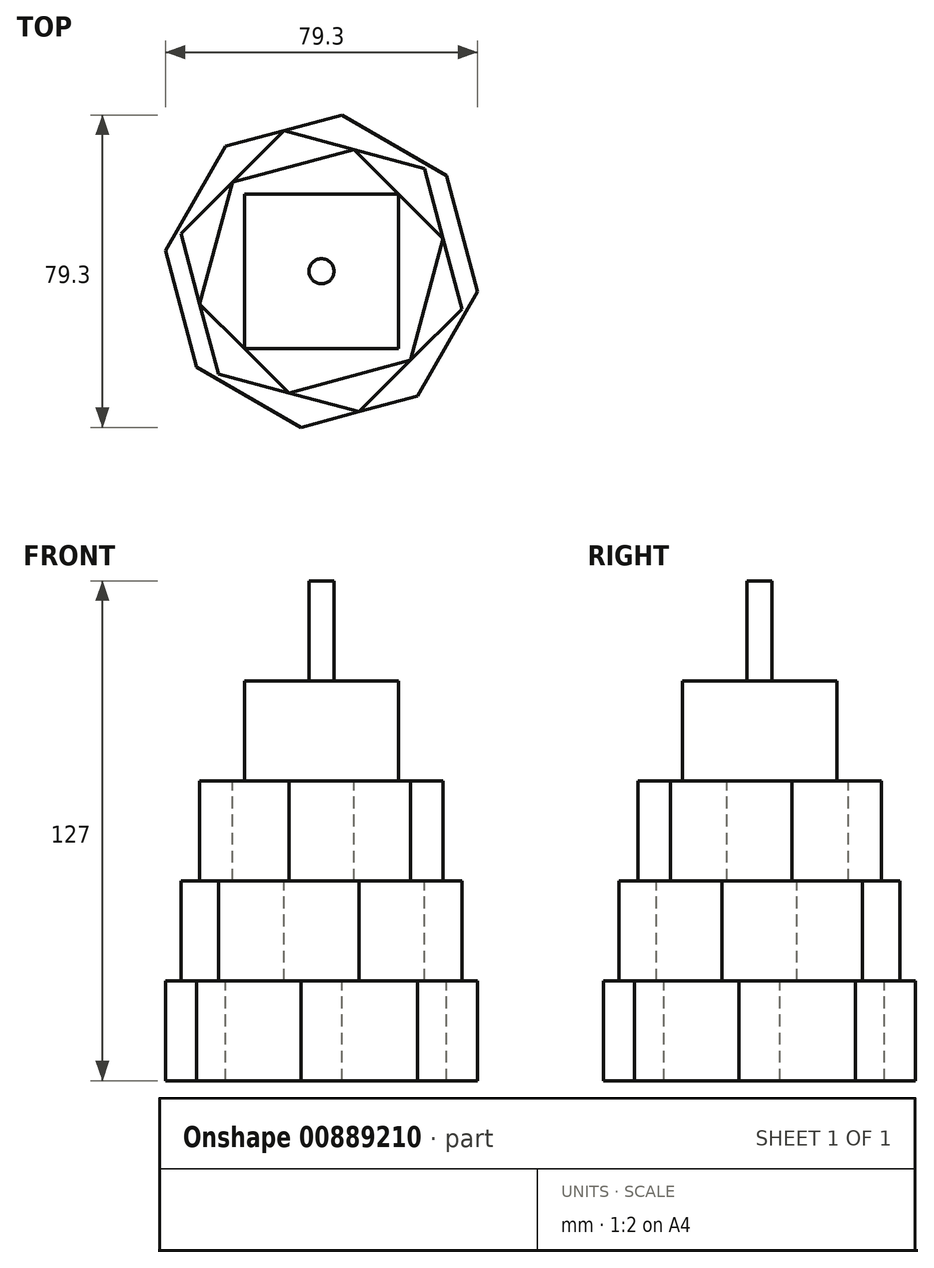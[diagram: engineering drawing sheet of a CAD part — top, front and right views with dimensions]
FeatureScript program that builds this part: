
annotation { "Feature Type Name" : "Feature", "Feature Type Description" : "" }
export const myFeature = defineFeature(function(context is Context, id is Id, definition is map)
    precondition{}
    {
        {
            var Q0;
            Q0=qCreatedBy(makeId("Top.planeOp"),FACE);
            var sketch = newSketch(context, id + "F0", { "sketchPlane" : qUnion([Q0])});
            skLineSegment(sketch, "E0.bottom", {"start": v(19.6, 19.6) * mm, "end": v(-19.6, 19.6) * mm});
            skLineSegment(sketch, "E0.top", {"start": v(19.6, -19.6) * mm, "end": v(-19.6, -19.6) * mm});
            skLineSegment(sketch, "E0.left", {"start": v(19.6, 19.6) * mm, "end": v(19.6, -19.6) * mm});
            skLineSegment(sketch, "E0.right", {"start": v(-19.6, 19.6) * mm, "end": v(-19.6, -19.6) * mm});
            skLineSegment(sketch, "E1.0", {"start": v(8.28, 30.9) * mm, "end": v(30.9, 8.28) * mm});
            skLineSegment(sketch, "E1.1", {"start": v(30.9, 8.28) * mm, "end": v(22.63, -22.63) * mm});
            skLineSegment(sketch, "E1.2", {"start": v(22.63, -22.63) * mm, "end": v(-8.28, -30.9) * mm});
            skLineSegment(sketch, "E1.3", {"start": v(-8.28, -30.9) * mm, "end": v(-30.9, -8.28) * mm});
            skLineSegment(sketch, "E1.4", {"start": v(-30.9, -8.28) * mm, "end": v(-22.63, 22.63) * mm});
            skLineSegment(sketch, "E1.5", {"start": v(-22.63, 22.63) * mm, "end": v(8.28, 30.9) * mm});
            skPoint(sketch, "E1.0.midPoint", {"position": v(19.6, 19.6) * mm});
            skLineSegment(sketch, "E2.0", {"start": v(-9.56, 35.69) * mm, "end": v(26.13, 26.13) * mm});
            skLineSegment(sketch, "E2.1", {"start": v(26.13, 26.13) * mm, "end": v(35.69, -9.56) * mm});
            skLineSegment(sketch, "E2.2", {"start": v(35.69, -9.56) * mm, "end": v(9.56, -35.69) * mm});
            skLineSegment(sketch, "E2.3", {"start": v(9.56, -35.69) * mm, "end": v(-26.13, -26.13) * mm});
            skLineSegment(sketch, "E2.4", {"start": v(-26.13, -26.13) * mm, "end": v(-35.69, 9.56) * mm});
            skLineSegment(sketch, "E2.5", {"start": v(-35.69, 9.56) * mm, "end": v(-9.56, 35.69) * mm});
            skPoint(sketch, "E2.0.midPoint", {"position": v(8.28, 30.9) * mm});
            skLineSegment(sketch, "E3.0", {"start": v(-24.35, 31.73) * mm, "end": v(5.22, 39.65) * mm});
            skLineSegment(sketch, "E3.1", {"start": v(5.22, 39.65) * mm, "end": v(31.73, 24.35) * mm});
            skLineSegment(sketch, "E3.2", {"start": v(31.73, 24.35) * mm, "end": v(39.65, -5.22) * mm});
            skLineSegment(sketch, "E3.3", {"start": v(39.65, -5.22) * mm, "end": v(24.35, -31.73) * mm});
            skLineSegment(sketch, "E3.4", {"start": v(24.35, -31.73) * mm, "end": v(-5.22, -39.65) * mm});
            skLineSegment(sketch, "E3.5", {"start": v(-5.22, -39.65) * mm, "end": v(-31.73, -24.35) * mm});
            skLineSegment(sketch, "E3.6", {"start": v(-31.73, -24.35) * mm, "end": v(-39.65, 5.22) * mm});
            skLineSegment(sketch, "E3.7", {"start": v(-39.65, 5.22) * mm, "end": v(-24.35, 31.73) * mm});
            skPoint(sketch, "E3.0.midPoint", {"position": v(-9.56, 35.69) * mm});
            skCircle(sketch, "E4", {"center": v(0, 0) * mm, "radius": 3.18 * mm});
            skSolve(sketch);
        }
        {
            var Q0;
            Q0 = qSketchRegion(id + "F0", true);
            var Q1;
            {var subQ0=sQuery(id+"F0.wireOp",EDGE,"E1.4");Q1=makeQuery(id+"F0.imprint","IMPRINT",FACE,{"disambiguationData":[TD([[makeQuery(id+"F0.imprint","IMPRINT",EDGE,{"derivedFrom":subQ0}),1.0]])]});}
            var Q2;
            {var subQ2=sQuery(id+"F0.wireOp",EDGE,"E2.3");var subQ4=sQuery(id+"F0.wireOp",EDGE,"E2.4");var subQ6=makeQuery(id+"F0.imprint","INTERSECT",VERTEX,{"derivedFrom":[subQ2,subQ4]});Q2=makeQuery(id+"F0.imprint","IMPRINT",FACE,{"disambiguationData":[TD([[makeQuery(id+"F0.imprint","IMPRINT",EDGE,{"disambiguationData":[TD([[subQ6,1.0]])],"derivedFrom":subQ2}),-1.0]])]});}
            var Q3;
            {var subQ3=sQuery(id+"F0.wireOp",EDGE,"E0.top");Q3=makeQuery(id+"F0.imprint","IMPRINT",FACE,{"disambiguationData":[TD([[makeQuery(id+"F0.imprint","IMPRINT",EDGE,{"derivedFrom":subQ3}),1.0]])]});}
            var Q4;
            {var subQ0=sQuery(id+"F0.wireOp",EDGE,"E1.1");Q4=makeQuery(id+"F0.imprint","IMPRINT",FACE,{"disambiguationData":[TD([[makeQuery(id+"F0.imprint","IMPRINT",EDGE,{"derivedFrom":subQ0}),1.0]])]});}
            var Q5;
            {var subQ2=sQuery(id+"F0.wireOp",EDGE,"E2.0");var subQ4=sQuery(id+"F0.wireOp",EDGE,"E2.1");var subQ6=makeQuery(id+"F0.imprint","INTERSECT",VERTEX,{"derivedFrom":[subQ2,subQ4]});Q5=makeQuery(id+"F0.imprint","IMPRINT",FACE,{"disambiguationData":[TD([[makeQuery(id+"F0.imprint","IMPRINT",EDGE,{"disambiguationData":[TD([[subQ6,1.0]])],"derivedFrom":subQ2}),-1.0]])]});}
            var Q6;
            {var subQ4=sQuery(id+"F0.wireOp",EDGE,"E0.bottom");Q6=makeQuery(id+"F0.imprint","IMPRINT",FACE,{"disambiguationData":[TD([[makeQuery(id+"F0.imprint","IMPRINT",EDGE,{"derivedFrom":subQ4}),-1.0]])]});}
            var Q7;
            Q7=makeQuery(id+"F0.imprint","IMPRINT",FACE,{"disambiguationData":[TD([[makeQuery(id+"F0.imprint","IMPRINT",EDGE,{"derivedFrom":sQuery(id+"F0.wireOp",EDGE,"E0.bottom")}),1.0]])]});
            var Q8;
            Q8=makeQuery(id+"F0.imprint","IMPRINT",FACE,{"disambiguationData":[TD([[makeQuery(id+"F0.imprint","IMPRINT",EDGE,{"derivedFrom":sQuery(id+"F0.wireOp",EDGE,"E4")}),1.0]])]});
            extrude(context, id + "F1", {"entities" : qUnion([Q0, Q1, Q2, Q3, Q4, Q5, Q6, Q7, Q8]), "oppositeDirection" : true, "depth" : 127 * mm, "offsetDistance" : 25.4 * mm});
        }
        {
            var Q0;
            {var subQ13=sQuery(id+"F0.wireOp",EDGE,"E3.5");Q0=makeQuery(id+"F0.imprint","IMPRINT",FACE,{"disambiguationData":[TD([[makeQuery(id+"F0.imprint","IMPRINT",EDGE,{"derivedFrom":subQ13}),-1.0]])]});}
            var Q1;
            {var subQ14=sQuery(id+"F0.wireOp",EDGE,"E3.1");Q1=makeQuery(id+"F0.imprint","IMPRINT",FACE,{"disambiguationData":[TD([[makeQuery(id+"F0.imprint","IMPRINT",EDGE,{"derivedFrom":subQ14}),-1.0]])]});}
            extrude(context, id + "F2", {"entities" : qUnion([Q0, Q1]), "operationType" : NewBodyOperationType.REMOVE, "oppositeDirection" : true, "depth" : 101.6 * mm, "offsetDistance" : 25.4 * mm});
        }
        {
            var Q0;
            {var subQ2=sQuery(id+"F0.wireOp",EDGE,"E2.3");var subQ4=sQuery(id+"F0.wireOp",EDGE,"E2.4");var subQ6=makeQuery(id+"F0.imprint","INTERSECT",VERTEX,{"derivedFrom":[subQ2,subQ4]});Q0=makeQuery(id+"F0.imprint","IMPRINT",FACE,{"disambiguationData":[TD([[makeQuery(id+"F0.imprint","IMPRINT",EDGE,{"disambiguationData":[TD([[subQ6,1.0]])],"derivedFrom":subQ2}),-1.0]])]});}
            var Q1;
            {var subQ0=sQuery(id+"F0.wireOp",EDGE,"E1.2");Q1=makeQuery(id+"F0.imprint","IMPRINT",FACE,{"disambiguationData":[TD([[makeQuery(id+"F0.imprint","IMPRINT",EDGE,{"derivedFrom":subQ0}),1.0]])]});}
            var Q2;
            {var subQ0=sQuery(id+"F0.wireOp",EDGE,"E1.1");Q2=makeQuery(id+"F0.imprint","IMPRINT",FACE,{"disambiguationData":[TD([[makeQuery(id+"F0.imprint","IMPRINT",EDGE,{"derivedFrom":subQ0}),1.0]])]});}
            var Q3;
            {var subQ2=sQuery(id+"F0.wireOp",EDGE,"E2.0");var subQ4=sQuery(id+"F0.wireOp",EDGE,"E2.1");var subQ6=makeQuery(id+"F0.imprint","INTERSECT",VERTEX,{"derivedFrom":[subQ2,subQ4]});Q3=makeQuery(id+"F0.imprint","IMPRINT",FACE,{"disambiguationData":[TD([[makeQuery(id+"F0.imprint","IMPRINT",EDGE,{"disambiguationData":[TD([[subQ6,1.0]])],"derivedFrom":subQ2}),-1.0]])]});}
            var Q4;
            {var subQ0=sQuery(id+"F0.wireOp",EDGE,"E1.5");Q4=makeQuery(id+"F0.imprint","IMPRINT",FACE,{"disambiguationData":[TD([[makeQuery(id+"F0.imprint","IMPRINT",EDGE,{"derivedFrom":subQ0}),1.0]])]});}
            var Q5;
            {var subQ0=sQuery(id+"F0.wireOp",EDGE,"E1.4");Q5=makeQuery(id+"F0.imprint","IMPRINT",FACE,{"disambiguationData":[TD([[makeQuery(id+"F0.imprint","IMPRINT",EDGE,{"derivedFrom":subQ0}),1.0]])]});}
            extrude(context, id + "F3", {"entities" : qUnion([Q0, Q1, Q2, Q3, Q4, Q5]), "operationType" : NewBodyOperationType.REMOVE, "oppositeDirection" : true, "depth" : 76.2 * mm, "offsetDistance" : 25.4 * mm});
        }
        {
            var Q0;
            {var subQ4=sQuery(id+"F0.wireOp",EDGE,"E0.bottom");Q0=makeQuery(id+"F0.imprint","IMPRINT",FACE,{"disambiguationData":[TD([[makeQuery(id+"F0.imprint","IMPRINT",EDGE,{"derivedFrom":subQ4}),-1.0]])]});}
            var Q1;
            {var subQ3=sQuery(id+"F0.wireOp",EDGE,"E0.top");Q1=makeQuery(id+"F0.imprint","IMPRINT",FACE,{"disambiguationData":[TD([[makeQuery(id+"F0.imprint","IMPRINT",EDGE,{"derivedFrom":subQ3}),1.0]])]});}
            extrude(context, id + "F4", {"entities" : qUnion([Q0, Q1]), "operationType" : NewBodyOperationType.REMOVE, "oppositeDirection" : true, "depth" : 50.8 * mm, "offsetDistance" : 25.4 * mm});
        }
        {
            var Q0;
            Q0=makeQuery(id+"F0.imprint","IMPRINT",FACE,{"disambiguationData":[TD([[makeQuery(id+"F0.imprint","IMPRINT",EDGE,{"derivedFrom":sQuery(id+"F0.wireOp",EDGE,"E0.bottom")}),1.0]])]});
            extrude(context, id + "F5", {"entities" : qUnion([Q0]), "operationType" : NewBodyOperationType.REMOVE, "oppositeDirection" : true, "depth" : 25.4 * mm, "offsetDistance" : 25.4 * mm});
        }
    });
